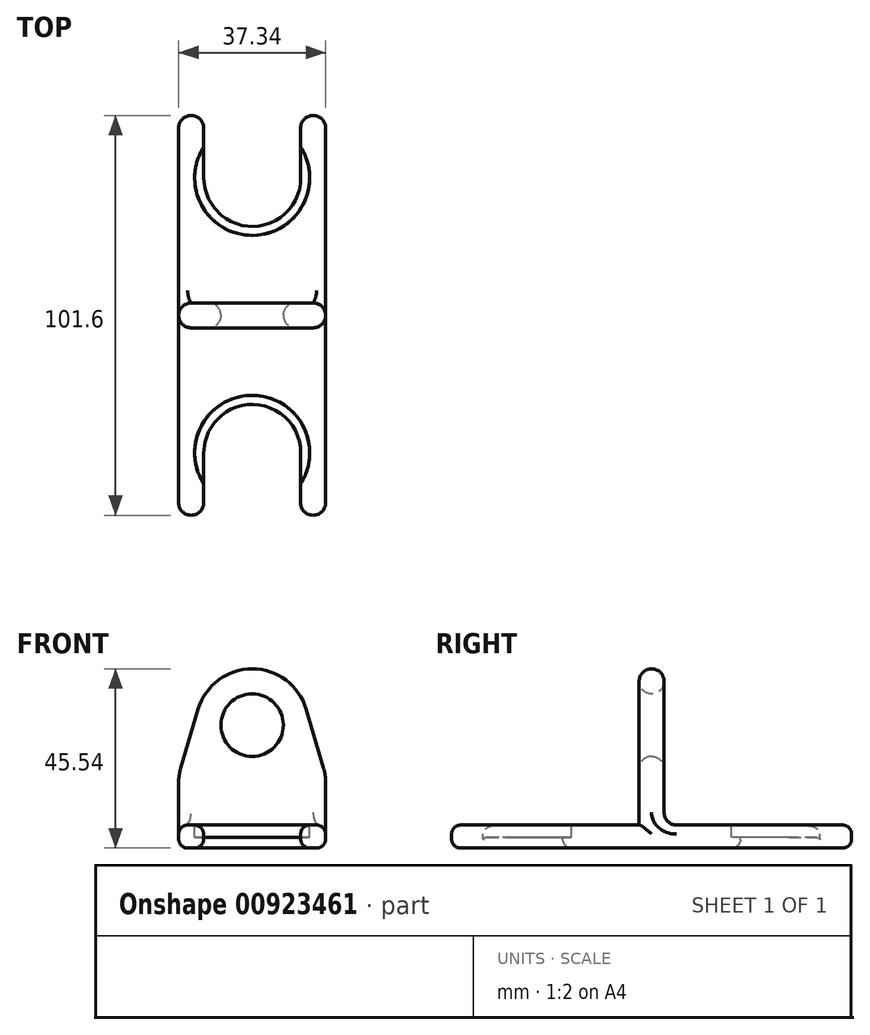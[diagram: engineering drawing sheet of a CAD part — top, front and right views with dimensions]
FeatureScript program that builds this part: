
annotation { "Feature Type Name" : "Feature", "Feature Type Description" : "" }
export const myFeature = defineFeature(function(context is Context, id is Id, definition is map)
    precondition{}
    {
        {
            var Q0;
            Q0=qCreatedBy(makeId("Top.planeOp"),FACE);
            var sketch = newSketch(context, id + "F0", { "sketchPlane" : qUnion([Q0])});
            skLineSegment(sketch, "E0", {"start": v(-12.32, -12.7) * mm, "end": v(-12.32, 0) * mm});
            skArc(sketch, "E1", {"start": v(0, 12.32) * mm, "mid": v(-8.71, 8.71) * mm, "end": v(-12.32, 0) * mm});
            skLineSegment(sketch, "E2", {"start": v(0, 36.67) * mm, "end": v(0, -49.3) * mm, "construction": true});
            skLineSegment(sketch, "E3.1", {"start": v(-18.67, -12.7) * mm, "end": v(-18.67, 0) * mm});
            skLineSegment(sketch, "E4", {"start": v(-15.5, -15.88) * mm, "end": v(-15.5, -15.88) * mm});
            skArc(sketch, "E5.MirrorCS", {"start": v(0, 12.32) * mm, "mid": v(8.71, 8.71) * mm, "end": v(12.32, 0) * mm});
            skLineSegment(sketch, "E6.MirrorCS", {"start": v(12.32, -12.7) * mm, "end": v(12.32, 0) * mm});
            skLineSegment(sketch, "E7.MirrorCS", {"start": v(18.67, -12.7) * mm, "end": v(18.67, 0) * mm});
            skLineSegment(sketch, "E8.MirrorCS", {"start": v(15.5, -15.88) * mm, "end": v(15.5, -15.88) * mm});
            skPoint(sketch, "E9.visualSharp", {"position": v(-18.67, -15.88) * mm});
            skArc(sketch, "E9.filletArc", {"start": v(-18.67, -12.7) * mm, "mid": v(-17.74, -14.95) * mm, "end": v(-15.5, -15.88) * mm});
            skPoint(sketch, "E10.visualSharp", {"position": v(-12.32, -15.88) * mm});
            skArc(sketch, "E10.filletArc", {"start": v(-15.5, -15.88) * mm, "mid": v(-13.25, -14.95) * mm, "end": v(-12.32, -12.7) * mm});
            skPoint(sketch, "E11.visualSharp", {"position": v(12.32, -15.88) * mm});
            skArc(sketch, "E11.filletArc", {"start": v(12.32, -12.7) * mm, "mid": v(13.25, -14.95) * mm, "end": v(15.5, -15.88) * mm});
            skPoint(sketch, "E12.visualSharp", {"position": v(18.67, -15.88) * mm});
            skArc(sketch, "E12.filletArc", {"start": v(15.5, -15.88) * mm, "mid": v(17.74, -14.95) * mm, "end": v(18.67, -12.7) * mm});
            skLineSegment(sketch, "E13", {"start": v(-18.67, 0) * mm, "end": v(-18.67, 34.92) * mm});
            skLineSegment(sketch, "E14", {"start": v(-18.67, 34.92) * mm, "end": v(18.67, 34.93) * mm});
            skLineSegment(sketch, "E15", {"start": v(18.67, 34.93) * mm, "end": v(18.67, 0) * mm});
            skSolve(sketch);
        }
        {
            var Q0;
            Q0=qSketchRegion(id+"F0",true);
            var Q1;
            Q1=qConstructionFilter(qBodyType(qCreatedBy(id+"F0",EDGE),BodyType.WIRE),ConstructionObject.NO);
            extrude(context, id + "F1", {"entities" : qUnion([Q0]), "surfaceEntities" : qUnion([Q1]), "oppositeDirection" : true, "depth" : 5.84 * mm, "offsetDistance" : 25.4 * mm});
        }
        {
            var Q0;
            Q0=makeQuery(id+"F1.opExtrude","CAP_FACE",FACE,{"disambiguationData":[OSD([sQuery(id+"F0.wireOp",EDGE,"E0"),sQuery(id+"F0.wireOp",EDGE,"E1"),sQuery(id+"F0.wireOp",EDGE,"E3.0"),sQuery(id+"F0.wireOp",EDGE,"E3.1"),sQuery(id+"F0.wireOp",EDGE,"59d09fa3-3ba2-4987-8950-9ce88f434f120.MirrorCS"),sQuery(id+"F0.wireOp",EDGE,"E5.MirrorCS"),sQuery(id+"F0.wireOp",EDGE,"E6.MirrorCS"),sQuery(id+"F0.wireOp",EDGE,"E7.MirrorCS"),sQuery(id+"F0.wireOp",EDGE,"E9.filletArc"),sQuery(id+"F0.wireOp",EDGE,"E10.filletArc"),sQuery(id+"F0.wireOp",EDGE,"E11.filletArc"),sQuery(id+"F0.wireOp",EDGE,"E12.filletArc")])],"isStart":true});
            var sketch = newSketch(context, id + "F2", { "sketchPlane" : qUnion([Q0])});
            skCircle(sketch, "E16", {"center": v(0, 0) * mm, "radius": 14.6 * mm});
            skSolve(sketch);
        }
        {
            var Q0;
            Q0=qSketchRegion(id+"F2",true);
            extrude(context, id + "F3", {"entities" : qUnion([Q0]), "operationType" : NewBodyOperationType.REMOVE, "oppositeDirection" : true, "depth" : 3.17 * mm, "offsetDistance" : 25.4 * mm});
        }
        {
            var Q0;
            Q0=makeQuery(id+"F1.opExtrude","SWEPT_BODY",BODY,{"disambiguationData":[OSD([sQuery(id+"F0.wireOp",EDGE,"E0"),sQuery(id+"F0.wireOp",EDGE,"E1"),sQuery(id+"F0.wireOp",EDGE,"E3.1"),sQuery(id+"F0.wireOp",EDGE,"E5.MirrorCS"),sQuery(id+"F0.wireOp",EDGE,"E6.MirrorCS"),sQuery(id+"F0.wireOp",EDGE,"E7.MirrorCS"),sQuery(id+"F0.wireOp",EDGE,"E9.filletArc"),sQuery(id+"F0.wireOp",EDGE,"E10.filletArc"),sQuery(id+"F0.wireOp",EDGE,"E11.filletArc"),sQuery(id+"F0.wireOp",EDGE,"E12.filletArc"),sQuery(id+"F0.wireOp",EDGE,"E13"),sQuery(id+"F0.wireOp",EDGE,"E14"),sQuery(id+"F0.wireOp",EDGE,"E15")])]});
            var Q1;
            Q1=makeQuery(id+"F1.opExtrude","SWEPT_FACE",FACE,{"disambiguationData":[OSD([sQuery(id+"F0.wireOp",EDGE,"E14")])]});
            mirror(context, id + "F4", {"operationType" : NewBodyOperationType.ADD, "entities" : qUnion([Q0]), "mirrorPlane" : qUnion([Q1])});
        }
        {
            var Q0;
            Q0=makeQuery(id+"F1.opExtrude","CAP_FACE",FACE,{"disambiguationData":[OSD([sQuery(id+"F0.wireOp",EDGE,"E0"),sQuery(id+"F0.wireOp",EDGE,"E1"),sQuery(id+"F0.wireOp",EDGE,"E3.1"),sQuery(id+"F0.wireOp",EDGE,"E5.MirrorCS"),sQuery(id+"F0.wireOp",EDGE,"E6.MirrorCS"),sQuery(id+"F0.wireOp",EDGE,"E7.MirrorCS"),sQuery(id+"F0.wireOp",EDGE,"E9.filletArc"),sQuery(id+"F0.wireOp",EDGE,"E10.filletArc"),sQuery(id+"F0.wireOp",EDGE,"E11.filletArc"),sQuery(id+"F0.wireOp",EDGE,"E12.filletArc"),sQuery(id+"F0.wireOp",EDGE,"E13"),sQuery(id+"F0.wireOp",EDGE,"E14"),sQuery(id+"F0.wireOp",EDGE,"E15")])],"isStart":true});
            var sketch = newSketch(context, id + "F5", { "sketchPlane" : qUnion([Q0])});
            skLineSegment(sketch, "E17.bottom", {"start": v(-18.67, 38.1) * mm, "end": v(18.67, 38.1) * mm});
            skLineSegment(sketch, "E17.top", {"start": v(-18.67, 31.75) * mm, "end": v(18.67, 31.75) * mm});
            skLineSegment(sketch, "E17.left", {"start": v(-18.67, 38.1) * mm, "end": v(-18.67, 31.75) * mm});
            skLineSegment(sketch, "E17.right", {"start": v(18.67, 38.1) * mm, "end": v(18.67, 31.75) * mm});
            skLineSegment(sketch, "E18", {"start": v(65.13, 34.93) * mm, "end": v(-27.8, 34.93) * mm, "construction": true});
            skSolve(sketch);
        }
        {
            var Q0;
            Q0=qSketchRegion(id+"F5",true);
            extrude(context, id + "F6", {"entities" : qUnion([Q0]), "operationType" : NewBodyOperationType.ADD, "depth" : 12.7 * mm, "offsetDistance" : 25.4 * mm});
        }
        {
            var Q0;
            Q0=makeQuery(id+"F6.opExtrude","SWEPT_FACE",FACE,{"disambiguationData":[OSD([sQuery(id+"F5.wireOp",EDGE,"E17.bottom")])]});
            var sketch = newSketch(context, id + "F7", { "sketchPlane" : qUnion([Q0])});
            skLineSegment(sketch, "E19", {"start": v(-18.67, 12.7) * mm, "end": v(-13.71, 29.46) * mm});
            skArc(sketch, "E20", {"start": v(0, 39.7) * mm, "mid": v(-8.56, 36.86) * mm, "end": v(-13.71, 29.46) * mm});
            skLineSegment(sketch, "E21", {"start": v(0, 0) * mm, "end": v(0, 48.46) * mm, "construction": true});
            skPoint(sketch, "E21.endSnap0", {"position": v(0, 7.93) * mm});
            skCircle(sketch, "E22", {"center": v(0, 25.4) * mm, "radius": 7.94 * mm});
            skLineSegment(sketch, "E23", {"start": v(-18.67, 12.7) * mm, "end": v(0, 12.7) * mm});
            skLineSegment(sketch, "E24.MirrorCS", {"start": v(18.67, 12.7) * mm, "end": v(0, 12.7) * mm});
            skLineSegment(sketch, "E25.MirrorCS", {"start": v(18.67, 12.7) * mm, "end": v(13.71, 29.46) * mm});
            skArc(sketch, "E26.MirrorCS", {"start": v(0, 39.7) * mm, "mid": v(8.56, 36.86) * mm, "end": v(13.71, 29.46) * mm});
            skSolve(sketch);
        }
        {
            var Q0;
            Q0=qSketchRegion(id+"F7",true);
            extrude(context, id + "F8", {"entities" : qUnion([Q0]), "operationType" : NewBodyOperationType.ADD, "oppositeDirection" : true, "depth" : 6.35 * mm, "offsetDistance" : 25.4 * mm});
        }
        {
            var Q0;
            {var subQ0=sQuery(id+"F5.wireOp",EDGE,"E17.right");Q0=makeQuery(id+"F8.boolean.opBoolean","MERGE",EDGE,{"derivedFrom":[makeQuery(id+"F6.opExtrude","CAP_EDGE",EDGE,{"disambiguationData":[OSD([subQ0])],"isStart":false}),makeQuery(id+"F8.opExtrude","SWEPT_EDGE",EDGE,{"disambiguationData":[OSD([sQuery(id+"F0.wireOp",EDGE,"E7.MirrorCS"),sQuery(id+"F0.wireOp",EDGE,"E15"),sQuery(id+"F5.wireOp",EDGE,"E17.bottom"),subQ0,sQuery(id+"F7.wireOp",EDGE,"E19"),sQuery(id+"F7.wireOp",EDGE,"E23")])]})]});}
            var Q1;
            {var subQ0=sQuery(id+"F5.wireOp",EDGE,"E17.left");Q1=makeQuery(id+"F8.boolean.opBoolean","MERGE",EDGE,{"derivedFrom":[makeQuery(id+"F6.opExtrude","CAP_EDGE",EDGE,{"disambiguationData":[OSD([subQ0])],"isStart":false}),makeQuery(id+"F8.opExtrude","SWEPT_EDGE",EDGE,{"disambiguationData":[OSD([sQuery(id+"F0.wireOp",EDGE,"E3.1"),sQuery(id+"F0.wireOp",EDGE,"E13"),sQuery(id+"F5.wireOp",EDGE,"E17.bottom"),subQ0,sQuery(id+"F7.wireOp",EDGE,"E24.MirrorCS"),sQuery(id+"F7.wireOp",EDGE,"E25.MirrorCS")])]})]});}
            fillet(context, id + "F9", {"entities" : qUnion([Q0, Q1]), "radius" : 12.7 * mm, "tangentPropagation" : true, "allowEdgeOverflow" : false});
        }
        {
            var Q0;
            Q0=makeQuery(id+"F1.opExtrude","CAP_EDGE",EDGE,{"disambiguationData":[OSD([sQuery(id+"F0.wireOp",EDGE,"E9.filletArc"),sQuery(id+"F0.wireOp",EDGE,"E10.filletArc")])],"isStart":true});
            var Q1;
            Q1=makeQuery(id+"F1.opExtrude","CAP_FACE",FACE,{"disambiguationData":[OSD([sQuery(id+"F0.wireOp",EDGE,"E0"),sQuery(id+"F0.wireOp",EDGE,"E1"),sQuery(id+"F0.wireOp",EDGE,"E3.1"),sQuery(id+"F0.wireOp",EDGE,"E5.MirrorCS"),sQuery(id+"F0.wireOp",EDGE,"E6.MirrorCS"),sQuery(id+"F0.wireOp",EDGE,"E7.MirrorCS"),sQuery(id+"F0.wireOp",EDGE,"E9.filletArc"),sQuery(id+"F0.wireOp",EDGE,"E10.filletArc"),sQuery(id+"F0.wireOp",EDGE,"E11.filletArc"),sQuery(id+"F0.wireOp",EDGE,"E12.filletArc"),sQuery(id+"F0.wireOp",EDGE,"E13"),sQuery(id+"F0.wireOp",EDGE,"E14"),sQuery(id+"F0.wireOp",EDGE,"E15")])],"isStart":false});
            var Q2;
            Q2=makeQuery(id+"F1.opExtrude","CAP_EDGE",EDGE,{"disambiguationData":[OSD([sQuery(id+"F0.wireOp",EDGE,"E11.filletArc"),sQuery(id+"F0.wireOp",EDGE,"E12.filletArc")])],"isStart":true});
            var Q3;
            Q3=makeQuery(id+"F4.opPattern","COPY",EDGE,{"derivedFrom":makeQuery(id+"F1.opExtrude","CAP_EDGE",EDGE,{"disambiguationData":[OSD([sQuery(id+"F0.wireOp",EDGE,"E11.filletArc"),sQuery(id+"F0.wireOp",EDGE,"E12.filletArc")])],"isStart":true}),"instanceName":"1"});
            var Q4;
            Q4=makeQuery(id+"F4.opPattern","COPY",EDGE,{"derivedFrom":makeQuery(id+"F1.opExtrude","CAP_EDGE",EDGE,{"disambiguationData":[OSD([sQuery(id+"F0.wireOp",EDGE,"E9.filletArc"),sQuery(id+"F0.wireOp",EDGE,"E10.filletArc")])],"isStart":true}),"instanceName":"1"});
            fillet(context, id + "F10", {"entities" : qUnion([Q0, Q1, Q2, Q3, Q4]), "radius" : 2.3 * mm, "tangentPropagation" : true, "allowEdgeOverflow" : false});
        }
        {
            var Q0;
            Q0=makeQuery(id+"F8.boolean.opBoolean","SPLIT",EDGE,{"derivedFrom":makeQuery(id+"Fg0FxBbyESaQHmS_1.opExtrude","CAP_EDGE",EDGE,{"disambiguationData":[OSD([sQuery(id+"FRgjImuMvHx0xUN_1.wireOp",EDGE,"mC6W0kxQ-4kdJ-szh7-Ajkx-FY7ZqaKWIjXH.right")])],"isStart":false})});
            var Q1;
            Q1=makeQuery(id+"F8.boolean.opBoolean","SPLIT",EDGE,{"derivedFrom":makeQuery(id+"Fg0FxBbyESaQHmS_1.opExtrude","CAP_EDGE",EDGE,{"disambiguationData":[OSD([sQuery(id+"FRgjImuMvHx0xUN_1.wireOp",EDGE,"mC6W0kxQ-4kdJ-szh7-Ajkx-FY7ZqaKWIjXH.left")])],"isStart":false})});
            var Q2;
            Q2=makeQuery(id+"Fg0FxBbyESaQHmS_1.boolean.opBoolean","MERGE",EDGE,{"derivedFrom":[makeQuery(id+"F6.boolean.opBoolean","MERGE",EDGE,{"derivedFrom":[makeQuery(id+"F1.opExtrude","SWEPT_EDGE",EDGE,{"disambiguationData":[OSD([sQuery(id+"F0.wireOp",EDGE,"E13"),sQuery(id+"F0.wireOp",EDGE,"E14")])]}),makeQuery(id+"F6.opExtrude","SWEPT_EDGE",EDGE,{"disambiguationData":[OSD([sQuery(id+"F5.wireOp",EDGE,"E17.bottom"),sQuery(id+"F5.wireOp",EDGE,"E17.left")])]})]}),makeQuery(id+"Fg0FxBbyESaQHmS_1.opExtrude","SWEPT_EDGE",EDGE,{"disambiguationData":[OSD([sQuery(id+"FRgjImuMvHx0xUN_1.wireOp",EDGE,"mC6W0kxQ-4kdJ-szh7-Ajkx-FY7ZqaKWIjXH.bottom"),sQuery(id+"FRgjImuMvHx0xUN_1.wireOp",EDGE,"mC6W0kxQ-4kdJ-szh7-Ajkx-FY7ZqaKWIjXH.right")])]})]});
            var Q3;
            Q3=makeQuery(id+"F6.opExtrude","SWEPT_EDGE",EDGE,{"disambiguationData":[OSD([sQuery(id+"F0.wireOp",EDGE,"E3.1"),sQuery(id+"F0.wireOp",EDGE,"E13"),sQuery(id+"F5.wireOp",EDGE,"E17.top"),sQuery(id+"F5.wireOp",EDGE,"E17.left")])]});
            var Q4;
            Q4=makeQuery(id+"F1.opExtrude","CAP_EDGE",EDGE,{"disambiguationData":[OSD([sQuery(id+"F0.wireOp",EDGE,"E14")])],"isStart":false});
            var Q5;
            Q5=makeQuery(id+"Fg0FxBbyESaQHmS_1.boolean.opBoolean","MERGE",EDGE,{"derivedFrom":[makeQuery(id+"F6.boolean.opBoolean","MERGE",EDGE,{"derivedFrom":[makeQuery(id+"F1.opExtrude","SWEPT_EDGE",EDGE,{"disambiguationData":[OSD([sQuery(id+"F0.wireOp",EDGE,"E14"),sQuery(id+"F0.wireOp",EDGE,"E15")])]}),makeQuery(id+"F6.opExtrude","SWEPT_EDGE",EDGE,{"disambiguationData":[OSD([sQuery(id+"F5.wireOp",EDGE,"E17.bottom"),sQuery(id+"F5.wireOp",EDGE,"E17.right")])]})]}),makeQuery(id+"Fg0FxBbyESaQHmS_1.opExtrude","SWEPT_EDGE",EDGE,{"disambiguationData":[OSD([sQuery(id+"FRgjImuMvHx0xUN_1.wireOp",EDGE,"mC6W0kxQ-4kdJ-szh7-Ajkx-FY7ZqaKWIjXH.bottom"),sQuery(id+"FRgjImuMvHx0xUN_1.wireOp",EDGE,"mC6W0kxQ-4kdJ-szh7-Ajkx-FY7ZqaKWIjXH.left")])]})]});
            var Q6;
            Q6=makeQuery(id+"F6.opExtrude","CAP_EDGE",EDGE,{"disambiguationData":[OSD([sQuery(id+"F5.wireOp",EDGE,"E17.bottom")])],"isStart":true});
            var Q7;
            Q7=makeQuery(id+"F8.opExtrude","CAP_EDGE",EDGE,{"disambiguationData":[OSD([sQuery(id+"F7.wireOp",EDGE,"E22")])],"isStart":true});
            var Q8;
            Q8=makeQuery(id+"F8.opExtrude","CAP_EDGE",EDGE,{"disambiguationData":[OSD([sQuery(id+"F7.wireOp",EDGE,"E22")])],"isStart":false});
            var Q9;
            Q9=makeQuery(id+"F6.opExtrude","CAP_EDGE",EDGE,{"disambiguationData":[OSD([sQuery(id+"F5.wireOp",EDGE,"E17.top")])],"isStart":true});
            fillet(context, id + "F11", {"entities" : qUnion([Q0, Q1, Q2, Q3, Q4, Q5, Q6, Q7, Q8, Q9]), "radius" : 3.17 * mm, "tangentPropagation" : true, "allowEdgeOverflow" : false});
        }
        {
            var Q0;
            Q0=makeQuery(id+"F3.boolean.opBoolean","COPY",EDGE,{"derivedFrom":makeQuery(id+"F3.opExtrude","CAP_EDGE",EDGE,{"disambiguationData":[OSD([sQuery(id+"F2.wireOp",EDGE,"E16")])],"isStart":true})});
            var Q1;
            Q1=makeQuery(id+"F4.opPattern","COPY",EDGE,{"derivedFrom":makeQuery(id+"F3.boolean.opBoolean","INTERSECT",EDGE,{"derivedFrom":[makeQuery(id+"F1.opExtrude","SWEPT_FACE",FACE,{"disambiguationData":[OSD([sQuery(id+"F0.wireOp",EDGE,"E1"),sQuery(id+"F0.wireOp",EDGE,"E5.MirrorCS")])]}),makeQuery(id+"F3.opExtrude","CAP_FACE",FACE,{"disambiguationData":[OSD([sQuery(id+"F2.wireOp",EDGE,"E16")])],"isStart":false})]}),"instanceName":"1"});
            var Q2;
            Q2=makeQuery(id+"F4.opPattern","COPY",EDGE,{"derivedFrom":makeQuery(id+"F3.boolean.opBoolean","COPY",EDGE,{"derivedFrom":makeQuery(id+"F3.opExtrude","CAP_EDGE",EDGE,{"disambiguationData":[OSD([sQuery(id+"F2.wireOp",EDGE,"E16")])],"isStart":true})}),"instanceName":"1"});
            var Q3;
            Q3=makeQuery(id+"F3.boolean.opBoolean","INTERSECT",EDGE,{"derivedFrom":[makeQuery(id+"F1.opExtrude","SWEPT_FACE",FACE,{"disambiguationData":[OSD([sQuery(id+"F0.wireOp",EDGE,"E1"),sQuery(id+"F0.wireOp",EDGE,"E5.MirrorCS")])]}),makeQuery(id+"F3.opExtrude","CAP_FACE",FACE,{"disambiguationData":[OSD([sQuery(id+"F2.wireOp",EDGE,"E16")])],"isStart":false})]});
            fillet(context, id + "F12", {"entities" : qUnion([Q0, Q1, Q2, Q3]), "radius" : 0.5 * mm, "tangentPropagation" : true, "allowEdgeOverflow" : false});
        }
    });
